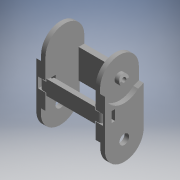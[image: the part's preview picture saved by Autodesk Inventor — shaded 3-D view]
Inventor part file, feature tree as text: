
AUTODESK INVENTOR PART (.ipt)
format: ipt  version: 2017.3 (Build 213256000, 256)  size: 296,960 bytes
history: native  units: mm (DEFAULTED — no unit token found)
features: other x84, extrude x17, sketch x17
ambient origin geometry x8: Origin, YZ Plane, XZ Plane, XY Plane, X Axis, Y Axis, Z Axis, Center Point
bodies: Solid1 (feature_tree)
feature tree (118):
  extrude  "Extrusion1"  Depth=158.0mm TaperAngle=0.0deg
  extrude  "Extrusion2"  Depth=18.0mm TaperAngle=0.0deg
  extrude  "Extrusion3"  Depth=60.0mm TaperAngle=0.0deg
  extrude  "Extrusion4"  Depth=60.0mm TaperAngle=0.0deg
  extrude  "Extrusion5"  Depth=52.0mm TaperAngle=0.0deg
  extrude  "Extrusion6"  Depth=9.0mm TaperAngle=0.0deg
  extrude  "Extrusion7"  Depth=9.0mm TaperAngle=0.0deg
  extrude  "Extrusion8"  Depth=8.181818mm TaperAngle=0.0deg
  extrude  "Extrusion9"  TaperAngle=0.0deg  [1 undecoded]
  extrude  "Extrusion10"  [1 undecoded]
  extrude  "Extrusion11"  [1 undecoded]
  extrude  "Extrusion12"  [1 undecoded]
  extrude  "Extrusion13"  [1 undecoded]
  extrude  "Extrusion14"  [1 undecoded]
  extrude  "Extrusion15"  [1 undecoded]
  extrude  "Extrusion16"  [1 undecoded]
  extrude  "Extrusion17"  [1 undecoded]
  other  "clip1_to_dummy_XY"
  other  "clip1_to_dummy_YZ"
  other  "clip1_to_dummy_ZX"
  other  "clip1_to_dummy_X"
  other  "clip1_to_dummy_Y"
  other  "clip1_to_dummy_Z"
  other  "clip1_to_dummy_Center"
  other  "clip_back_to_clip_front_XY"
  other  "clip_back_to_clip_front_YZ"
  other  "clip_back_to_clip_front_ZX"
  other  "clip_back_to_clip_front_X"
  other  "clip_back_to_clip_front_Y"
  other  "clip_back_to_clip_front_Z"
  other  "clip_back_to_clip_front_Center"
  other  "clip_end_to_fitting_free_left_XY"
  other  "clip_end_to_fitting_free_left_YZ"
  other  "clip_end_to_fitting_free_left_ZX"
  other  "clip_end_to_fitting_free_left_X"
  other  "clip_end_to_fitting_free_left_Y"
  other  "clip_end_to_fitting_free_left_Z"
  other  "clip_end_to_fitting_free_left_Center"
  other  "clip_end_to_fitting_free_right_XY"
  other  "clip_end_to_fitting_free_right_YZ"
  other  "clip_end_to_fitting_free_right_ZX"
  other  "clip_end_to_fitting_free_right_X"
  other  "clip_end_to_fitting_free_right_Y"
  other  "clip_end_to_fitting_free_right_Z"
  other  "clip_end_to_fitting_free_right_Center"
  other  "clip_front_to_clip_back_XY"
  other  "clip_front_to_clip_back_YZ"
  other  "clip_front_to_clip_back_ZX"
  other  "clip_front_to_clip_back_X"
  other  "clip_front_to_clip_back_Y"
  other  "clip_front_to_clip_back_Z"
  other  "clip_front_to_clip_back_Center"
  other  "clip_front_to_fitting_fixed_left_XY"
  other  "clip_front_to_fitting_fixed_left_YZ"
  other  "clip_front_to_fitting_fixed_left_ZX"
  other  "clip_front_to_fitting_fixed_left_X"
  other  "clip_front_to_fitting_fixed_left_Y"
  other  "clip_front_to_fitting_fixed_left_Z"
  other  "clip_front_to_fitting_fixed_left_Center"
  other  "clip_front_to_fitting_fixed_right_XY"
  other  "clip_front_to_fitting_fixed_right_YZ"
  other  "clip_front_to_fitting_fixed_right_ZX"
  other  "clip_front_to_fitting_fixed_right_X"
  other  "clip_front_to_fitting_fixed_right_Y"
  other  "clip_front_to_fitting_fixed_right_Z"
  other  "clip_front_to_fitting_fixed_right_Center"
  other  "clip_front_to_fitting_right_XY"
  other  "clip_front_to_fitting_right_YZ"
  other  "clip_front_to_fitting_right_ZX"
  other  "clip_front_to_fitting_right_X"
  other  "clip_front_to_fitting_right_Y"
  other  "clip_front_to_fitting_right_Z"
  other  "clip_front_to_fitting_right_Center"
  other  "clip_to_flap_XY"
  other  "clip_to_flap_YZ"
  other  "clip_to_flap_ZX"
  other  "clip_to_flap_X"
  other  "clip_to_flap_Y"
  other  "clip_to_flap_Z"
  other  "clip_to_flap_Center"
  other  "to_center_XY"
  other  "to_center_YZ"
  other  "to_center_ZX"
  other  "to_center_X"
  other  "to_center_Y"
  other  "to_center_Z"
  other  "to_center_Center"
  other  "to_clip1_XY"
  other  "to_clip1_YZ"
  other  "to_clip1_ZX"
  other  "to_clip1_X"
  other  "to_clip1_Y"
  other  "to_clip1_Z"
  other  "to_clip1_Center"
  other  "to_clip5_XY"
  other  "to_clip5_YZ"
  other  "to_clip5_ZX"
  other  "to_clip5_X"
  other  "to_clip5_Y"
  other  "to_clip5_Z"
  other  "to_clip5_Center"
  sketch  "Sketch_1"  dims[d0=79.0mm d1=0.0mm d2=158.0mm d3=0.0mm]
  sketch  "Sketch_3"  dims[d8=60.0mm d9=0.0mm d10=15.0mm d11=0.0mm]
  sketch  "Sketch_6"  dims[d20=15.0mm d21=0.0mm d22=9.0mm d23=0.0mm]
  sketch  "Sketch_4"  dims[d12=15.0mm d13=0.0mm d14=60.0mm d15=0.0mm]
  sketch  "Sketch_2"  dims[d4=18.0mm d5=0.0mm d6=158.0mm d7=0.0mm]
  sketch  "Sketch_5"  dims[d16=52.0mm d17=0.0mm d18=15.0mm d19=0.0mm]
  sketch  "Sketch_8"  dims[d28=8.5mm d29=0.0mm d30=8.181818mm d31=0.0mm]
  sketch  "Sketch_11"
  sketch  "Sketch_24"
  sketch  "Sketch_7"  dims[d24=9.0mm d25=0.0mm d26=8.5mm d27=0.0mm]
  sketch  "Sketch_9"  dims[d32=12.857143mm d33=0.0mm d34=0.0mm d35=0.0mm]
  sketch  "Sketch_10"
  sketch  "Sketch_13"
  sketch  "Sketch_14"
  sketch  "Sketch_18"
  sketch  "Sketch_25"
  sketch  "Sketch_27"
note: 9 required parameter values undecoded (feature->parameter linkage not recoverable at this tier; creation-order binding heuristic only, values carry confidence <= 0.55)
